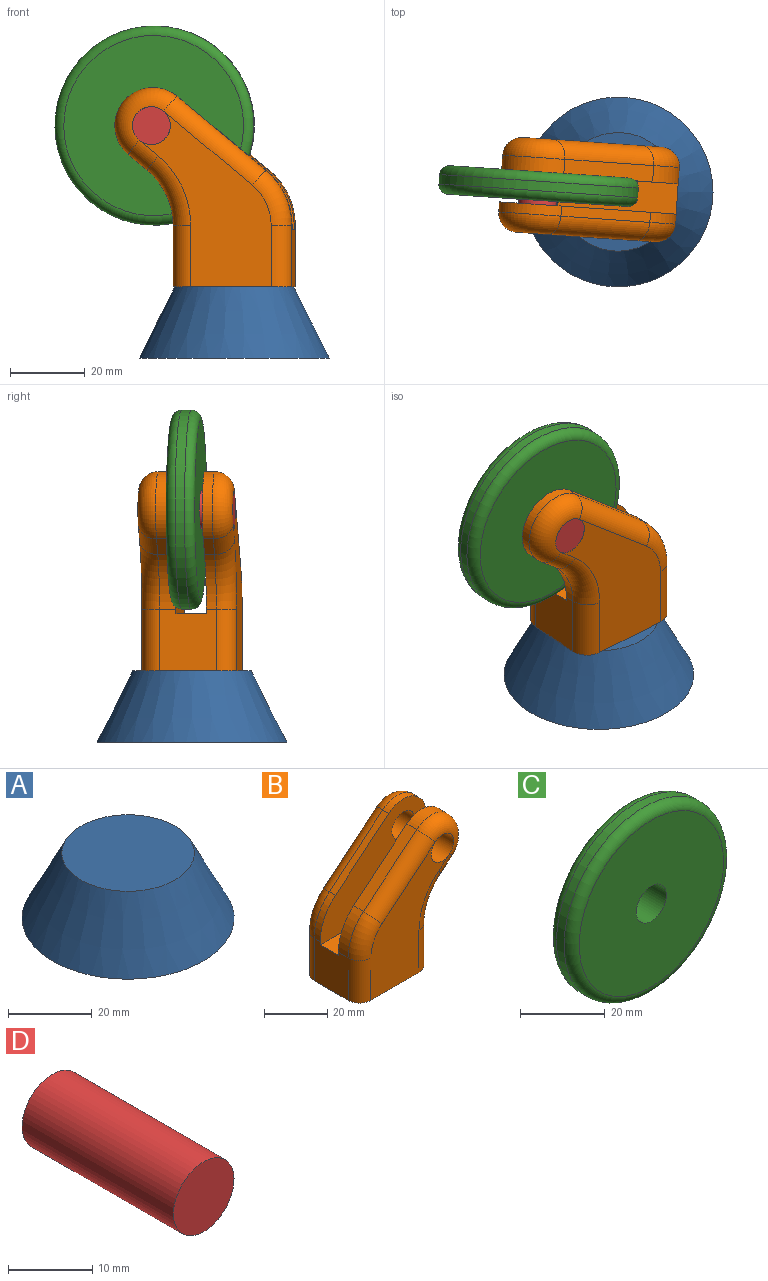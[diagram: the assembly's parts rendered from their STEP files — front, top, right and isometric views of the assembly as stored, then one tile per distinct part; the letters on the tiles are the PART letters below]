
ASSEMBLY  parts=4 mates=3
PART A: 3 faces, bbox 50.8x50.8x19.1 mm
  f0: plane 50.8x50.8mm, normal (0,0,-1), area 2026.8mm2, adj f2
  f1: plane 31.75x31.75mm, normal (0,0,1), area 791.7mm2, adj f2
  f2: cone r=25.4mm half-angle=26.6deg, axis (0,0,-1), area 2761.8mm2, adj f0,f1
PART B: 34 faces, bbox 49.8x25.4x54.2 mm
  f0: plane 23.86x19.87mm, normal (-0.64,0,0.77), area 83.9mm2, adj f1,f5,f21,f33
  f1: cylinder r=19.05mm len=14.64mm, axis (0,1,0), area 45.1mm2, adj f0,f8,f22,f33
  f2: cylinder r=19.05mm len=14.64mm, axis (0,1,0), area 45.1mm2, adj f3,f10,f18,f33
  f3: plane 5.12x4.26mm, normal (0.64,0,-0.77), area 18mm2, adj f2,f5,f19,f33
  f4: cylinder r=5.08mm len=10.16mm, axis (0,1,0), area 248.3mm2, adj f16,f20,f33
  f5: cylinder r=10.16mm len=17.97mm, axis (0,1,0), area 86.2mm2, adj f0,f3,f20,f33
  f6: plane 23.86x19.87mm, normal (-0.64,0,0.77), area 137mm2, adj f7,f14,f28,f32
  f7: cylinder r=19.05mm len=14.64mm, axis (0,1,0), area 73.6mm2, adj f6,f8,f29,f32
  f8: plane 16.47x15.24mm, normal (-1,0,0), area 241mm2, adj f1,f7,f9,f23,f30,f31,f32,f33
  f9: plane 31.75x25.4mm, normal (0,0,-1), area 784.3mm2, adj f8,f10,f15,f16,f17,f23,f24,f30
  f10: plane 16.47x15.24mm, normal (1,0,0), area 241mm2, adj f2,f9,f11,f17,f24,f31,f32,f33
  f11: cylinder r=19.05mm len=14.64mm, axis (0,1,0), area 73.6mm2, adj f10,f12,f25,f32
  f12: plane 5.12x4.41mm, normal (0.64,0,-0.77), area 29.4mm2, adj f11,f14,f26,f32
  f13: cylinder r=5.08mm len=10.16mm, axis (0,1,0), area 303mm2, adj f15,f27,f32
  f14: cylinder r=10.16mm len=17.97mm, axis (0,1,0), area 140.8mm2, adj f6,f12,f27,f32
  f15: plane 47.08x35.39mm, normal (0,-1,0), area 801.9mm2, adj f9,f13,f24,f25,f26,f28,f29,f30
  f16: plane 47.08x35.39mm, normal (0,1,0), area 801.9mm2, adj f4,f9,f17,f18,f19,f21,f22,f23
  f17: cylinder r=5.08mm len=16.47mm, axis (0,0,1), area 131.5mm2, adj f9,f10,f16,f18
  f18: torus R=24.13mm, axis (0,-1,0), area 146.1mm2, adj f2,f16,f17,f19
  f19: cylinder r=5.08mm len=8.37mm, axis (0.77,0,0.64), area 53.1mm2, adj f3,f16,f18,f20
  f20: torus R=5.08mm, axis (0,-1,0), area 208.4mm2, adj f4,f5,f19,f21
  f21: cylinder r=5.08mm len=27.11mm, axis (-0.77,0,-0.64), area 247.8mm2, adj f0,f16,f20,f22
  f22: torus R=13.97mm, axis (0,-1,0), area 120.3mm2, adj f1,f16,f21,f23
  f23: cylinder r=5.08mm len=16.47mm, axis (0,0,-1), area 131.5mm2, adj f8,f9,f16,f22
  f24: cylinder r=5.08mm len=16.47mm, axis (0,0,-1), area 131.5mm2, adj f9,f10,f15,f25
  f25: torus R=24.13mm, axis (0,-1,0), area 146.1mm2, adj f11,f15,f24,f26
  f26: cylinder r=5.08mm len=8.37mm, axis (-0.77,0,-0.64), area 53.1mm2, adj f12,f15,f25,f27
  f27: torus R=5.08mm, axis (0,-1,0), area 208.4mm2, adj f13,f14,f26,f28
  f28: cylinder r=5.08mm len=27.11mm, axis (0.77,0,0.64), area 247.8mm2, adj f6,f15,f27,f29
  f29: torus R=13.97mm, axis (0,-1,0), area 120.3mm2, adj f7,f15,f28,f30
  f30: cylinder r=5.08mm len=16.47mm, axis (0,0,1), area 131.5mm2, adj f8,f9,f15,f29
  f31: plane 31.75x8.13mm, normal (0,0,1), area 258.1mm2, adj f8,f10,f32,f33
  f32: plane 47.38x38.1mm, normal (0,1,0), area 968.2mm2, adj f6,f7,f8,f10,f11,f12,f13,f14
  f33: plane 47.38x38.1mm, normal (0,-1,0), area 968.2mm2, adj f0,f1,f2,f3,f4,f5,f8,f10
PART C: 6 faces, bbox 57.7x7.6x57.7 mm
  f0: cylinder r=26.67mm len=53.34mm, axis (0,1,0), area 425.6mm2, adj f3,f4
  f1: plane 48.26x48.26mm, normal (0,-1,0), area 1748.1mm2, adj f4,f5
  f2: plane 48.26x48.26mm, normal (0,1,0), area 1748.1mm2, adj f3,f5
  f3: torus R=24.13mm, axis (0,-1,0), area 645.4mm2, adj f0,f2
  f4: torus R=24.13mm, axis (0,-1,0), area 645.4mm2, adj f0,f1
  f5: cylinder r=5.08mm len=10.16mm, axis (0,-1,0), area 243.2mm2, adj f1,f2
PART D: 3 faces, bbox 10.2x25.4x10.2 mm
  f0: cylinder r=5.08mm len=25.4mm, axis (0,1,0), area 810.7mm2, adj f1,f2
  f1: plane 10.16x10.16mm, normal (0,-1,0), area 81.1mm2, adj f0
  f2: plane 10.16x10.16mm, normal (0,1,0), area 81.1mm2, adj f0
PLACE A at identity fixed
PLACE B rot(axis=(0,0,1),176.1deg) t=(0,0,0)mm
PLACE C rot(axis=(-0.99,0.03,0.13),179.5deg) t=(-25.88,1.77,127.86)mm
PLACE D rot(axis=(-0.99,0.03,0.13),179.5deg) t=(-25.88,1.77,127.86)mm
MATE revolute A.f2 <-> B.f9  axis (0,0,1) through (0,0,19.05)mm
MATE fastened C.f0 <-> D.f0  axis (0.07,1,0) through (-21.3,1.46,62.23)mm
MATE revolute B.f4 <-> D.f0  axis (-0.07,-1,0) through (-20.43,14.13,62.23)mm
